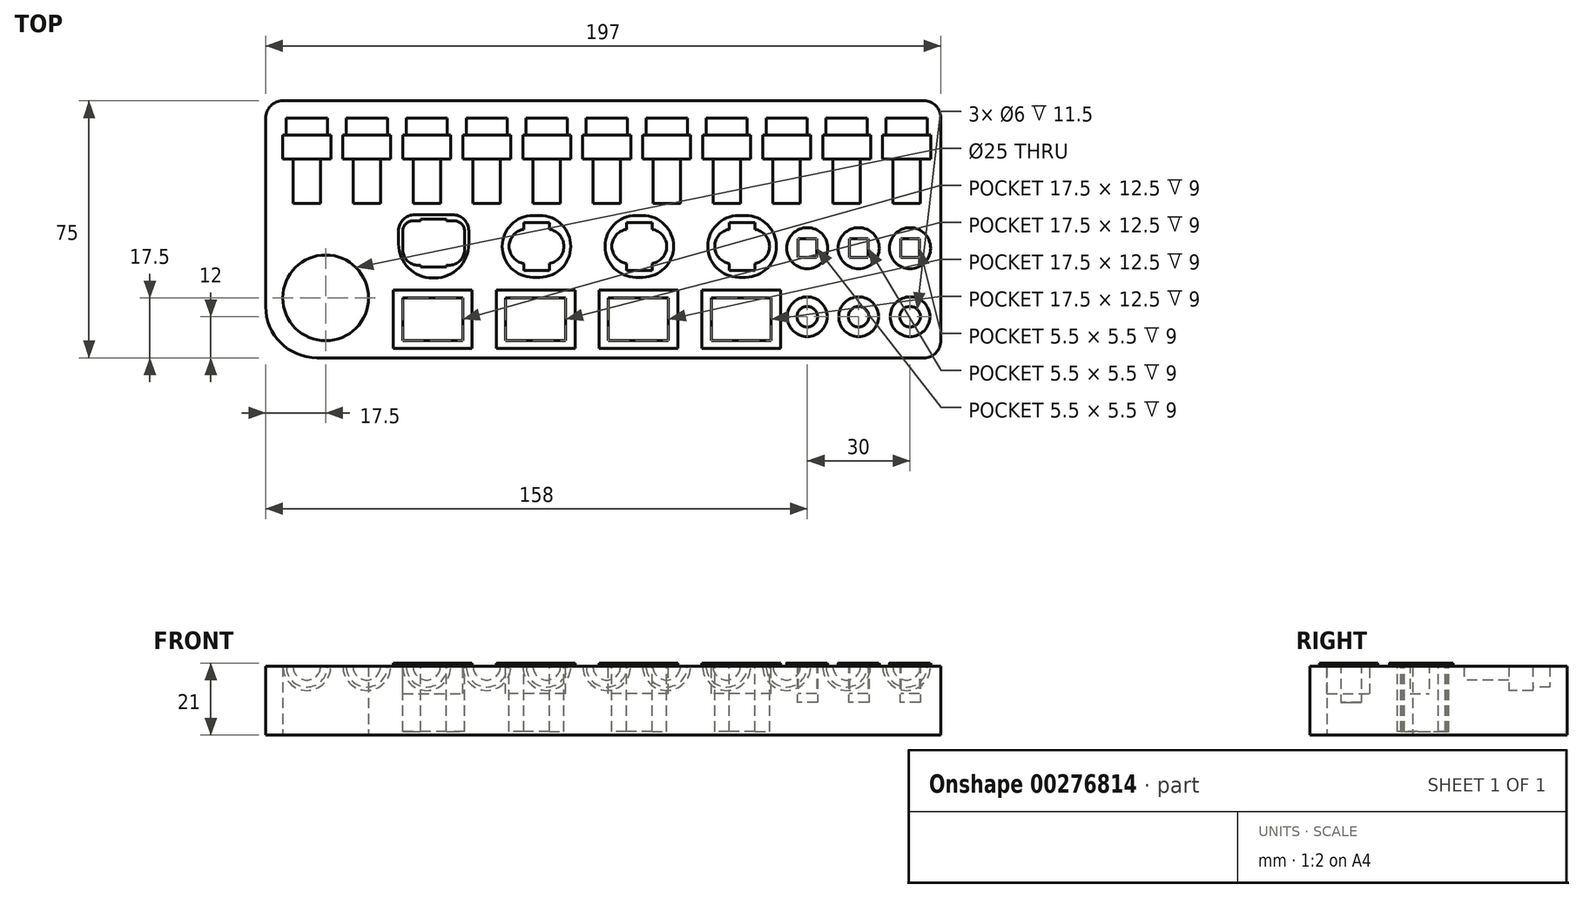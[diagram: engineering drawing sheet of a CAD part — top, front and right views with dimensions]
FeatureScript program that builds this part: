
annotation { "Feature Type Name" : "Feature", "Feature Type Description" : "" }
export const myFeature = defineFeature(function(context is Context, id is Id, definition is map)
    precondition{}
    {
        {
            var Q0;
            Q0=qCreatedBy(makeId("Top.planeOp"),FACE);
            var sketch = newSketch(context, id + "F0", { "sketchPlane" : qUnion([Q0])});
            skLineSegment(sketch, "E0.bottom", {"start": v(15, 0) * mm, "end": v(192, 0) * mm});
            skLineSegment(sketch, "E0.top", {"start": v(5, 75) * mm, "end": v(192, 75) * mm});
            skLineSegment(sketch, "E0.left", {"start": v(0, 15) * mm, "end": v(0, 70) * mm});
            skLineSegment(sketch, "E0.right", {"start": v(197, 5) * mm, "end": v(197, 70) * mm});
            skPoint(sketch, "E1.visualSharp", {"position": v(0, 0) * mm});
            skArc(sketch, "E1.filletArc", {"start": v(0, 15) * mm, "mid": v(4.4, 4.4) * mm, "end": v(15, 0) * mm});
            skPoint(sketch, "E2.visualSharp", {"position": v(0, 75) * mm});
            skArc(sketch, "E2.filletArc", {"start": v(5, 75) * mm, "mid": v(1.46, 73.54) * mm, "end": v(0, 70) * mm});
            skPoint(sketch, "E3.visualSharp", {"position": v(197, 75) * mm});
            skArc(sketch, "E3.filletArc", {"start": v(197, 70) * mm, "mid": v(195.54, 73.54) * mm, "end": v(192, 75) * mm});
            skPoint(sketch, "E4.visualSharp", {"position": v(197, 0) * mm});
            skArc(sketch, "E4.filletArc", {"start": v(192, 0) * mm, "mid": v(195.54, 1.46) * mm, "end": v(197, 5) * mm});
            skLineSegment(sketch, "E5.bottom", {"start": v(0, 0) * mm, "end": v(17.5, 0) * mm, "construction": true});
            skLineSegment(sketch, "E5.top", {"start": v(0, 17.5) * mm, "end": v(17.5, 17.5) * mm, "construction": true});
            skLineSegment(sketch, "E5.left", {"start": v(0, 0) * mm, "end": v(0, 17.5) * mm, "construction": true});
            skLineSegment(sketch, "E5.right", {"start": v(17.5, 0) * mm, "end": v(17.5, 17.5) * mm, "construction": true});
            skCircle(sketch, "E6", {"center": v(17.5, 17.5) * mm, "radius": 12.5 * mm});
            skSolve(sketch);
        }
        {
            var Q0;
            Q0=qSketchRegion(id+"F0",true);
            extrude(context, id + "F1", {"entities" : qUnion([Q0]), "depth" : 20 * mm});
        }
        {
            var Q0;
            Q0=makeQuery(id+"F1.opExtrude","CAP_FACE",FACE,{"disambiguationData":[OSD([sQuery(id+"F0.wireOp",EDGE,"E0.bottom"),sQuery(id+"F0.wireOp",EDGE,"E0.top"),sQuery(id+"F0.wireOp",EDGE,"E0.left"),sQuery(id+"F0.wireOp",EDGE,"E0.right"),sQuery(id+"F0.wireOp",EDGE,"E1.filletArc"),sQuery(id+"F0.wireOp",EDGE,"E2.filletArc"),sQuery(id+"F0.wireOp",EDGE,"E3.filletArc"),sQuery(id+"F0.wireOp",EDGE,"E4.filletArc"),sQuery(id+"F0.wireOp",EDGE,"E6")])],"isStart":false});
            var sketch = newSketch(context, id + "F2", { "sketchPlane" : qUnion([Q0])});
            skLineSegment(sketch, "E7.bottom", {"start": v(0, 0) * mm, "end": v(12, 0) * mm, "construction": true});
            skLineSegment(sketch, "E7.top", {"start": v(0, 70) * mm, "end": v(12, 70) * mm, "construction": true});
            skLineSegment(sketch, "E7.left", {"start": v(0, 0) * mm, "end": v(0, 70) * mm, "construction": true});
            skLineSegment(sketch, "E7.right", {"start": v(12, 0) * mm, "end": v(12, 70) * mm, "construction": true});
            skLineSegment(sketch, "E8", {"start": v(12, 70) * mm, "end": v(29.5, 70) * mm, "construction": true});
            skLineSegment(sketch, "E9", {"start": v(29.5, 70) * mm, "end": v(47, 70) * mm, "construction": true});
            skLineSegment(sketch, "E10", {"start": v(47, 70) * mm, "end": v(64.5, 70) * mm, "construction": true});
            skLineSegment(sketch, "E11", {"start": v(64.5, 70) * mm, "end": v(82, 70) * mm, "construction": true});
            skLineSegment(sketch, "E12", {"start": v(82, 70) * mm, "end": v(99.5, 70) * mm, "construction": true});
            skLineSegment(sketch, "E13", {"start": v(99.5, 70) * mm, "end": v(117, 70) * mm, "construction": true});
            skLineSegment(sketch, "E14", {"start": v(117, 70) * mm, "end": v(134.5, 70) * mm, "construction": true});
            skLineSegment(sketch, "E15", {"start": v(134.5, 70) * mm, "end": v(152, 70) * mm, "construction": true});
            skLineSegment(sketch, "E16", {"start": v(152, 70) * mm, "end": v(169.5, 70) * mm, "construction": true});
            skLineSegment(sketch, "E17", {"start": v(169.5, 70) * mm, "end": v(187, 70) * mm, "construction": true});
            skLineSegment(sketch, "E18.bottom", {"start": v(12, 70) * mm, "end": v(18, 70) * mm});
            skLineSegment(sketch, "E18.left", {"start": v(12, 70) * mm, "end": v(12, 65) * mm});
            skLineSegment(sketch, "E18.right", {"start": v(18, 70) * mm, "end": v(18, 65) * mm});
            skLineSegment(sketch, "E19.bottom", {"start": v(29.5, 70) * mm, "end": v(35.5, 70) * mm});
            skLineSegment(sketch, "E19.left", {"start": v(29.5, 70) * mm, "end": v(29.5, 65) * mm});
            skLineSegment(sketch, "E19.right", {"start": v(35.5, 70) * mm, "end": v(35.5, 65) * mm});
            skLineSegment(sketch, "E20.bottom", {"start": v(47, 70) * mm, "end": v(53, 70) * mm});
            skLineSegment(sketch, "E20.left", {"start": v(47, 70) * mm, "end": v(47, 65) * mm});
            skLineSegment(sketch, "E20.right", {"start": v(53, 70) * mm, "end": v(53, 65) * mm});
            skLineSegment(sketch, "E21.bottom", {"start": v(64.5, 70) * mm, "end": v(70.5, 70) * mm});
            skLineSegment(sketch, "E21.left", {"start": v(64.5, 70) * mm, "end": v(64.5, 65) * mm});
            skLineSegment(sketch, "E21.right", {"start": v(70.5, 70) * mm, "end": v(70.5, 65) * mm});
            skLineSegment(sketch, "E22.bottom", {"start": v(82, 70) * mm, "end": v(88, 70) * mm});
            skLineSegment(sketch, "E22.left", {"start": v(82, 70) * mm, "end": v(82, 65) * mm});
            skLineSegment(sketch, "E22.right", {"start": v(88, 70) * mm, "end": v(88, 65) * mm});
            skLineSegment(sketch, "E23.bottom", {"start": v(99.5, 70) * mm, "end": v(105.5, 70) * mm});
            skLineSegment(sketch, "E23.left", {"start": v(99.5, 70) * mm, "end": v(99.5, 65) * mm});
            skLineSegment(sketch, "E23.right", {"start": v(105.5, 70) * mm, "end": v(105.5, 65) * mm});
            skLineSegment(sketch, "E24.bottom", {"start": v(117, 70) * mm, "end": v(123, 70) * mm});
            skLineSegment(sketch, "E24.left", {"start": v(117, 70) * mm, "end": v(117, 65) * mm});
            skLineSegment(sketch, "E24.right", {"start": v(123, 70) * mm, "end": v(123, 65) * mm});
            skLineSegment(sketch, "E25.bottom", {"start": v(134.5, 70) * mm, "end": v(140.5, 70) * mm});
            skLineSegment(sketch, "E25.left", {"start": v(134.5, 70) * mm, "end": v(134.5, 65) * mm});
            skLineSegment(sketch, "E25.right", {"start": v(140.5, 70) * mm, "end": v(140.5, 65) * mm});
            skLineSegment(sketch, "E26.bottom", {"start": v(152, 70) * mm, "end": v(158, 70) * mm});
            skLineSegment(sketch, "E26.left", {"start": v(152, 70) * mm, "end": v(152, 65) * mm});
            skLineSegment(sketch, "E26.right", {"start": v(158, 70) * mm, "end": v(158, 65) * mm});
            skLineSegment(sketch, "E27.bottom", {"start": v(169.5, 70) * mm, "end": v(175.5, 70) * mm});
            skLineSegment(sketch, "E27.left", {"start": v(169.5, 70) * mm, "end": v(169.5, 65) * mm});
            skLineSegment(sketch, "E27.right", {"start": v(175.5, 70) * mm, "end": v(175.5, 65) * mm});
            skLineSegment(sketch, "E28.bottom", {"start": v(187, 70) * mm, "end": v(193, 70) * mm});
            skLineSegment(sketch, "E28.left", {"start": v(187, 70) * mm, "end": v(187, 65) * mm});
            skLineSegment(sketch, "E28.right", {"start": v(193, 70) * mm, "end": v(193, 65) * mm});
            skLineSegment(sketch, "E29.bottom", {"start": v(18, 65) * mm, "end": v(19, 65) * mm});
            skLineSegment(sketch, "E29.top", {"start": v(16, 58) * mm, "end": v(19, 58) * mm});
            skLineSegment(sketch, "E29.left", {"start": v(12, 65) * mm, "end": v(12, 58) * mm});
            skLineSegment(sketch, "E29.right", {"start": v(19, 65) * mm, "end": v(19, 58) * mm});
            skLineSegment(sketch, "E30.bottom", {"start": v(35.5, 65) * mm, "end": v(36.5, 65) * mm});
            skLineSegment(sketch, "E30.top", {"start": v(33.5, 58) * mm, "end": v(36.5, 58) * mm});
            skLineSegment(sketch, "E30.left", {"start": v(29.5, 65) * mm, "end": v(29.5, 58) * mm});
            skLineSegment(sketch, "E30.right", {"start": v(36.5, 65) * mm, "end": v(36.5, 58) * mm});
            skLineSegment(sketch, "E31.bottom", {"start": v(53, 65) * mm, "end": v(54, 65) * mm});
            skLineSegment(sketch, "E31.top", {"start": v(51, 58) * mm, "end": v(54, 58) * mm});
            skLineSegment(sketch, "E31.left", {"start": v(47, 65) * mm, "end": v(47, 58) * mm});
            skLineSegment(sketch, "E31.right", {"start": v(54, 65) * mm, "end": v(54, 58) * mm});
            skLineSegment(sketch, "E32.bottom", {"start": v(70.5, 65) * mm, "end": v(71.5, 65) * mm});
            skLineSegment(sketch, "E32.top", {"start": v(68.5, 58) * mm, "end": v(71.5, 58) * mm});
            skLineSegment(sketch, "E32.left", {"start": v(64.5, 65) * mm, "end": v(64.5, 58) * mm});
            skLineSegment(sketch, "E32.right", {"start": v(71.5, 65) * mm, "end": v(71.5, 58) * mm});
            skLineSegment(sketch, "E33.bottom", {"start": v(88, 65) * mm, "end": v(89, 65) * mm});
            skLineSegment(sketch, "E33.top", {"start": v(86, 58) * mm, "end": v(89, 58) * mm});
            skLineSegment(sketch, "E33.left", {"start": v(82, 65) * mm, "end": v(82, 58) * mm});
            skLineSegment(sketch, "E33.right", {"start": v(89, 65) * mm, "end": v(89, 58) * mm});
            skLineSegment(sketch, "E34.bottom", {"start": v(105.5, 65) * mm, "end": v(106.5, 65) * mm});
            skLineSegment(sketch, "E34.top", {"start": v(103.5, 58) * mm, "end": v(106.5, 58) * mm});
            skLineSegment(sketch, "E34.left", {"start": v(99.5, 65) * mm, "end": v(99.5, 58) * mm});
            skLineSegment(sketch, "E34.right", {"start": v(106.5, 65) * mm, "end": v(106.5, 58) * mm});
            skLineSegment(sketch, "E35.bottom", {"start": v(123, 65) * mm, "end": v(124, 65) * mm});
            skLineSegment(sketch, "E35.top", {"start": v(121, 58) * mm, "end": v(124, 58) * mm});
            skLineSegment(sketch, "E35.left", {"start": v(117, 65) * mm, "end": v(117, 58) * mm});
            skLineSegment(sketch, "E35.right", {"start": v(124, 65) * mm, "end": v(124, 58) * mm});
            skLineSegment(sketch, "E36.bottom", {"start": v(140.5, 65) * mm, "end": v(141.5, 65) * mm});
            skLineSegment(sketch, "E36.top", {"start": v(138.5, 58) * mm, "end": v(141.5, 58) * mm});
            skLineSegment(sketch, "E36.left", {"start": v(134.5, 65) * mm, "end": v(134.5, 58) * mm});
            skLineSegment(sketch, "E36.right", {"start": v(141.5, 65) * mm, "end": v(141.5, 58) * mm});
            skLineSegment(sketch, "E37.top", {"start": v(156, 58) * mm, "end": v(159, 58) * mm});
            skLineSegment(sketch, "E37.left", {"start": v(152, 65) * mm, "end": v(152, 58) * mm});
            skLineSegment(sketch, "E37.right", {"start": v(159, 65) * mm, "end": v(159, 58) * mm});
            skLineSegment(sketch, "E38.bottom", {"start": v(175.5, 65) * mm, "end": v(176.5, 65) * mm});
            skLineSegment(sketch, "E38.top", {"start": v(173.5, 58) * mm, "end": v(176.5, 58) * mm});
            skLineSegment(sketch, "E38.left", {"start": v(169.5, 65) * mm, "end": v(169.5, 58) * mm});
            skLineSegment(sketch, "E38.right", {"start": v(176.5, 65) * mm, "end": v(176.5, 58) * mm});
            skLineSegment(sketch, "E39.bottom", {"start": v(193, 65) * mm, "end": v(194, 65) * mm});
            skLineSegment(sketch, "E39.top", {"start": v(191, 58) * mm, "end": v(194, 58) * mm});
            skLineSegment(sketch, "E39.left", {"start": v(187, 65) * mm, "end": v(187, 58) * mm});
            skLineSegment(sketch, "E39.right", {"start": v(194, 65) * mm, "end": v(194, 58) * mm});
            skLineSegment(sketch, "E40.top", {"start": v(12, 45) * mm, "end": v(16, 45) * mm});
            skLineSegment(sketch, "E40.left", {"start": v(12, 58) * mm, "end": v(12, 45) * mm});
            skLineSegment(sketch, "E40.right", {"start": v(16, 58) * mm, "end": v(16, 45) * mm});
            skLineSegment(sketch, "E41.top", {"start": v(29.5, 45) * mm, "end": v(33.5, 45) * mm});
            skLineSegment(sketch, "E41.left", {"start": v(29.5, 58) * mm, "end": v(29.5, 45) * mm});
            skLineSegment(sketch, "E41.right", {"start": v(33.5, 58) * mm, "end": v(33.5, 45) * mm});
            skLineSegment(sketch, "E42.top", {"start": v(47, 45) * mm, "end": v(51, 45) * mm});
            skLineSegment(sketch, "E42.left", {"start": v(47, 58) * mm, "end": v(47, 45) * mm});
            skLineSegment(sketch, "E42.right", {"start": v(51, 58) * mm, "end": v(51, 45) * mm});
            skLineSegment(sketch, "E43.top", {"start": v(64.5, 45) * mm, "end": v(68.5, 45) * mm});
            skLineSegment(sketch, "E43.left", {"start": v(64.5, 58) * mm, "end": v(64.5, 45) * mm});
            skLineSegment(sketch, "E43.right", {"start": v(68.5, 58) * mm, "end": v(68.5, 45) * mm});
            skLineSegment(sketch, "E44.top", {"start": v(82, 45) * mm, "end": v(86, 45) * mm});
            skLineSegment(sketch, "E44.left", {"start": v(82, 58) * mm, "end": v(82, 45) * mm});
            skLineSegment(sketch, "E44.right", {"start": v(86, 58) * mm, "end": v(86, 45) * mm});
            skLineSegment(sketch, "E45.top", {"start": v(99.5, 45) * mm, "end": v(103.5, 45) * mm});
            skLineSegment(sketch, "E45.left", {"start": v(99.5, 58) * mm, "end": v(99.5, 45) * mm});
            skLineSegment(sketch, "E45.right", {"start": v(103.5, 58) * mm, "end": v(103.5, 45) * mm});
            skLineSegment(sketch, "E46.top", {"start": v(117, 45) * mm, "end": v(121, 45) * mm});
            skLineSegment(sketch, "E46.left", {"start": v(117, 58) * mm, "end": v(117, 45) * mm});
            skLineSegment(sketch, "E46.right", {"start": v(121, 58) * mm, "end": v(121, 45) * mm});
            skLineSegment(sketch, "E47.top", {"start": v(134.5, 45) * mm, "end": v(138.5, 45) * mm});
            skLineSegment(sketch, "E47.left", {"start": v(134.5, 58) * mm, "end": v(134.5, 45) * mm});
            skLineSegment(sketch, "E47.right", {"start": v(138.5, 58) * mm, "end": v(138.5, 45) * mm});
            skLineSegment(sketch, "E48.top", {"start": v(152, 45) * mm, "end": v(156, 45) * mm});
            skLineSegment(sketch, "E48.left", {"start": v(152, 58) * mm, "end": v(152, 45) * mm});
            skLineSegment(sketch, "E48.right", {"start": v(156, 58) * mm, "end": v(156, 45) * mm});
            skLineSegment(sketch, "E49.top", {"start": v(169.5, 45) * mm, "end": v(173.5, 45) * mm});
            skLineSegment(sketch, "E49.left", {"start": v(169.5, 58) * mm, "end": v(169.5, 45) * mm});
            skLineSegment(sketch, "E49.right", {"start": v(173.5, 58) * mm, "end": v(173.5, 45) * mm});
            skLineSegment(sketch, "E50.top", {"start": v(187, 45) * mm, "end": v(191, 45) * mm});
            skLineSegment(sketch, "E50.left", {"start": v(187, 58) * mm, "end": v(187, 45) * mm});
            skLineSegment(sketch, "E50.right", {"start": v(191, 58) * mm, "end": v(191, 45) * mm});
            skLineSegment(sketch, "E51", {"start": v(158, 65) * mm, "end": v(159, 65) * mm});
            skSolve(sketch);
        }
        {
            var Q0;
            Q0=makeQuery(id+"F2.imprint","IMPRINT",FACE,{"disambiguationData":[TD([[makeQuery(id+"F2.imprint","IMPRINT",EDGE,{"derivedFrom":sQuery(id+"F2.wireOp",EDGE,"E18.bottom")}),-1.0]])]});
            var Q1;
            Q1=sQuery(id+"F2.wireOp",EDGE,"E40.left");
            revolve(context, id + "F3", {"operationType" : NewBodyOperationType.REMOVE, "entities" : qUnion([Q0]), "axis" : qUnion([Q1]), "revolveType" : RevolveType.FULL, "oppositeDirection" : true});
        }
        {
            var Q0;
            Q0=makeQuery(id+"F2.imprint","IMPRINT",FACE,{"disambiguationData":[TD([[makeQuery(id+"F2.imprint","IMPRINT",EDGE,{"derivedFrom":sQuery(id+"F2.wireOp",EDGE,"E19.bottom")}),-1.0]])]});
            var Q1;
            Q1=sQuery(id+"F2.wireOp",EDGE,"E41.left");
            revolve(context, id + "F4", {"operationType" : NewBodyOperationType.REMOVE, "entities" : qUnion([Q0]), "axis" : qUnion([Q1]), "revolveType" : RevolveType.FULL, "oppositeDirection" : true});
        }
        {
            var Q0;
            Q0=makeQuery(id+"F2.imprint","IMPRINT",FACE,{"disambiguationData":[TD([[makeQuery(id+"F2.imprint","IMPRINT",EDGE,{"derivedFrom":sQuery(id+"F2.wireOp",EDGE,"E20.bottom")}),-1.0]])]});
            var Q1;
            Q1=sQuery(id+"F2.wireOp",EDGE,"E42.left");
            revolve(context, id + "F5", {"operationType" : NewBodyOperationType.REMOVE, "entities" : qUnion([Q0]), "axis" : qUnion([Q1]), "revolveType" : RevolveType.FULL, "oppositeDirection" : true});
        }
        {
            var Q0;
            Q0=makeQuery(id+"F2.imprint","IMPRINT",FACE,{"disambiguationData":[TD([[makeQuery(id+"F2.imprint","IMPRINT",EDGE,{"derivedFrom":sQuery(id+"F2.wireOp",EDGE,"E21.bottom")}),-1.0]])]});
            var Q1;
            Q1=sQuery(id+"F2.wireOp",EDGE,"E43.left");
            revolve(context, id + "F6", {"operationType" : NewBodyOperationType.REMOVE, "entities" : qUnion([Q0]), "axis" : qUnion([Q1]), "revolveType" : RevolveType.FULL, "oppositeDirection" : true});
        }
        {
            var Q0;
            Q0=makeQuery(id+"F2.imprint","IMPRINT",FACE,{"disambiguationData":[TD([[makeQuery(id+"F2.imprint","IMPRINT",EDGE,{"derivedFrom":sQuery(id+"F2.wireOp",EDGE,"E22.bottom")}),-1.0]])]});
            var Q1;
            Q1=sQuery(id+"F2.wireOp",EDGE,"E44.left");
            revolve(context, id + "F7", {"operationType" : NewBodyOperationType.REMOVE, "entities" : qUnion([Q0]), "axis" : qUnion([Q1]), "revolveType" : RevolveType.FULL, "oppositeDirection" : true});
        }
        {
            var Q0;
            Q0=makeQuery(id+"F2.imprint","IMPRINT",FACE,{"disambiguationData":[TD([[makeQuery(id+"F2.imprint","IMPRINT",EDGE,{"derivedFrom":sQuery(id+"F2.wireOp",EDGE,"E23.bottom")}),-1.0]])]});
            var Q1;
            Q1=sQuery(id+"F2.wireOp",EDGE,"E45.left");
            revolve(context, id + "F8", {"operationType" : NewBodyOperationType.REMOVE, "entities" : qUnion([Q0]), "axis" : qUnion([Q1]), "revolveType" : RevolveType.FULL, "oppositeDirection" : true});
        }
        {
            var Q0;
            Q0=makeQuery(id+"F2.imprint","IMPRINT",FACE,{"disambiguationData":[TD([[makeQuery(id+"F2.imprint","IMPRINT",EDGE,{"derivedFrom":sQuery(id+"F2.wireOp",EDGE,"E24.bottom")}),-1.0]])]});
            var Q1;
            Q1=sQuery(id+"F2.wireOp",EDGE,"E46.left");
            revolve(context, id + "F9", {"operationType" : NewBodyOperationType.REMOVE, "entities" : qUnion([Q0]), "axis" : qUnion([Q1]), "revolveType" : RevolveType.FULL, "oppositeDirection" : true});
        }
        {
            var Q0;
            Q0=makeQuery(id+"F2.imprint","IMPRINT",FACE,{"disambiguationData":[TD([[makeQuery(id+"F2.imprint","IMPRINT",EDGE,{"derivedFrom":sQuery(id+"F2.wireOp",EDGE,"E25.bottom")}),-1.0]])]});
            var Q1;
            Q1=sQuery(id+"F2.wireOp",EDGE,"E47.left");
            revolve(context, id + "F10", {"operationType" : NewBodyOperationType.REMOVE, "entities" : qUnion([Q0]), "axis" : qUnion([Q1]), "revolveType" : RevolveType.FULL, "oppositeDirection" : true});
        }
        {
            var Q0;
            Q0=makeQuery(id+"F2.imprint","IMPRINT",FACE,{"disambiguationData":[TD([[makeQuery(id+"F2.imprint","IMPRINT",EDGE,{"derivedFrom":sQuery(id+"F2.wireOp",EDGE,"E27.bottom")}),-1.0]])]});
            var Q1;
            Q1=sQuery(id+"F2.wireOp",EDGE,"E49.left");
            revolve(context, id + "F11", {"operationType" : NewBodyOperationType.REMOVE, "entities" : qUnion([Q0]), "axis" : qUnion([Q1]), "revolveType" : RevolveType.FULL, "oppositeDirection" : true});
        }
        {
            var Q0;
            Q0=makeQuery(id+"F2.imprint","IMPRINT",FACE,{"disambiguationData":[TD([[makeQuery(id+"F2.imprint","IMPRINT",EDGE,{"derivedFrom":sQuery(id+"F2.wireOp",EDGE,"E26.bottom")}),-1.0]])]});
            var Q1;
            Q1=sQuery(id+"F2.wireOp",EDGE,"E48.left");
            revolve(context, id + "F12", {"operationType" : NewBodyOperationType.REMOVE, "entities" : qUnion([Q0]), "axis" : qUnion([Q1]), "revolveType" : RevolveType.FULL, "oppositeDirection" : true});
        }
        {
            var Q0;
            Q0=makeQuery(id+"F2.imprint","IMPRINT",FACE,{"disambiguationData":[TD([[makeQuery(id+"F2.imprint","IMPRINT",EDGE,{"derivedFrom":sQuery(id+"F2.wireOp",EDGE,"E28.bottom")}),-1.0]])]});
            var Q1;
            Q1=sQuery(id+"F2.wireOp",EDGE,"E50.left");
            revolve(context, id + "F13", {"operationType" : NewBodyOperationType.REMOVE, "entities" : qUnion([Q0]), "axis" : qUnion([Q1]), "revolveType" : RevolveType.FULL, "oppositeDirection" : true});
        }
        {
            var Q0;
            Q0=makeQuery(id+"F1.opExtrude","CAP_FACE",FACE,{"disambiguationData":[OSD([sQuery(id+"F0.wireOp",EDGE,"E0.bottom"),sQuery(id+"F0.wireOp",EDGE,"E0.top"),sQuery(id+"F0.wireOp",EDGE,"E0.left"),sQuery(id+"F0.wireOp",EDGE,"E0.right"),sQuery(id+"F0.wireOp",EDGE,"E1.filletArc"),sQuery(id+"F0.wireOp",EDGE,"E2.filletArc"),sQuery(id+"F0.wireOp",EDGE,"E3.filletArc"),sQuery(id+"F0.wireOp",EDGE,"E4.filletArc"),sQuery(id+"F0.wireOp",EDGE,"E6")])],"isStart":false});
            var sketch = newSketch(context, id + "F14", { "sketchPlane" : qUnion([Q0])});
            skLineSegment(sketch, "E52.bottom", {"start": v(0, 0) * mm, "end": v(40, 0) * mm, "construction": true});
            skLineSegment(sketch, "E52.top", {"start": v(0, 5) * mm, "end": v(40, 5) * mm, "construction": true});
            skLineSegment(sketch, "E52.left", {"start": v(0, 0) * mm, "end": v(0, 5) * mm, "construction": true});
            skLineSegment(sketch, "E52.right", {"start": v(40, 0) * mm, "end": v(40, 5) * mm, "construction": true});
            skLineSegment(sketch, "E53.bottom", {"start": v(40, 5) * mm, "end": v(57.5, 5) * mm});
            skLineSegment(sketch, "E53.top", {"start": v(40, 17.5) * mm, "end": v(57.5, 17.5) * mm});
            skLineSegment(sketch, "E53.left", {"start": v(40, 5) * mm, "end": v(40, 17.5) * mm});
            skLineSegment(sketch, "E53.right", {"start": v(57.5, 5) * mm, "end": v(57.5, 17.5) * mm});
            skLineSegment(sketch, "E54", {"start": v(57.5, 17.5) * mm, "end": v(87.5, 17.5) * mm, "construction": true});
            skLineSegment(sketch, "E55", {"start": v(87.5, 17.5) * mm, "end": v(117.5, 17.5) * mm, "construction": true});
            skLineSegment(sketch, "E56", {"start": v(117.5, 17.5) * mm, "end": v(147.5, 17.5) * mm, "construction": true});
            skLineSegment(sketch, "E57.bottom", {"start": v(87.5, 17.5) * mm, "end": v(70, 17.5) * mm});
            skLineSegment(sketch, "E57.top", {"start": v(87.5, 5) * mm, "end": v(70, 5) * mm});
            skLineSegment(sketch, "E57.left", {"start": v(87.5, 17.5) * mm, "end": v(87.5, 5) * mm});
            skLineSegment(sketch, "E57.right", {"start": v(70, 17.5) * mm, "end": v(70, 5) * mm});
            skLineSegment(sketch, "E58.bottom", {"start": v(117.5, 17.5) * mm, "end": v(100, 17.5) * mm});
            skLineSegment(sketch, "E58.top", {"start": v(117.5, 5) * mm, "end": v(100, 5) * mm});
            skLineSegment(sketch, "E58.left", {"start": v(117.5, 17.5) * mm, "end": v(117.5, 5) * mm});
            skLineSegment(sketch, "E58.right", {"start": v(100, 17.5) * mm, "end": v(100, 5) * mm});
            skLineSegment(sketch, "E59.bottom", {"start": v(147.5, 17.5) * mm, "end": v(130, 17.5) * mm});
            skLineSegment(sketch, "E59.top", {"start": v(147.5, 5) * mm, "end": v(130, 5) * mm});
            skLineSegment(sketch, "E59.left", {"start": v(147.5, 17.5) * mm, "end": v(147.5, 5) * mm});
            skLineSegment(sketch, "E59.right", {"start": v(130, 17.5) * mm, "end": v(130, 5) * mm});
            skLineSegment(sketch, "E60", {"start": v(40, 5) * mm, "end": v(57.5, 17.5) * mm, "construction": true});
            skLineSegment(sketch, "E61", {"start": v(70, 17.5) * mm, "end": v(87.5, 5) * mm, "construction": true});
            skLineSegment(sketch, "E62", {"start": v(100, 5) * mm, "end": v(117.5, 17.5) * mm, "construction": true});
            skLineSegment(sketch, "E63", {"start": v(130, 17.5) * mm, "end": v(147.5, 5) * mm, "construction": true});
            skLineSegment(sketch, "E64.bottom", {"start": v(60.25, 2.75) * mm, "end": v(37.25, 2.75) * mm});
            skLineSegment(sketch, "E64.top", {"start": v(60.25, 19.75) * mm, "end": v(37.25, 19.75) * mm});
            skLineSegment(sketch, "E64.left", {"start": v(60.25, 2.75) * mm, "end": v(60.25, 19.75) * mm});
            skLineSegment(sketch, "E64.right", {"start": v(37.25, 2.75) * mm, "end": v(37.25, 19.75) * mm});
            skPoint(sketch, "E64.middle", {"position": v(48.75, 11.25) * mm});
            skLineSegment(sketch, "E65.bottom", {"start": v(67.25, 2.75) * mm, "end": v(90.25, 2.75) * mm});
            skLineSegment(sketch, "E65.top", {"start": v(67.25, 19.75) * mm, "end": v(90.25, 19.75) * mm});
            skLineSegment(sketch, "E65.left", {"start": v(67.25, 2.75) * mm, "end": v(67.25, 19.75) * mm});
            skLineSegment(sketch, "E65.right", {"start": v(90.25, 2.75) * mm, "end": v(90.25, 19.75) * mm});
            skPoint(sketch, "E65.middle", {"position": v(78.75, 11.25) * mm});
            skLineSegment(sketch, "E66.bottom", {"start": v(97.25, 19.75) * mm, "end": v(120.25, 19.75) * mm});
            skLineSegment(sketch, "E66.top", {"start": v(97.25, 2.75) * mm, "end": v(120.25, 2.75) * mm});
            skLineSegment(sketch, "E66.left", {"start": v(97.25, 19.75) * mm, "end": v(97.25, 2.75) * mm});
            skLineSegment(sketch, "E66.right", {"start": v(120.25, 19.75) * mm, "end": v(120.25, 2.75) * mm});
            skPoint(sketch, "E66.middle", {"position": v(108.75, 11.25) * mm});
            skLineSegment(sketch, "E67.bottom", {"start": v(127.25, 2.75) * mm, "end": v(150.25, 2.75) * mm});
            skLineSegment(sketch, "E67.top", {"start": v(127.25, 19.75) * mm, "end": v(150.25, 19.75) * mm});
            skLineSegment(sketch, "E67.left", {"start": v(127.25, 2.75) * mm, "end": v(127.25, 19.75) * mm});
            skLineSegment(sketch, "E67.right", {"start": v(150.25, 2.75) * mm, "end": v(150.25, 19.75) * mm});
            skPoint(sketch, "E67.middle", {"position": v(138.75, 11.25) * mm});
            skSolve(sketch);
        }
        {
            var Q0;
            Q0=makeQuery(id+"F14.imprint","IMPRINT",FACE,{"disambiguationData":[TD([[makeQuery(id+"F14.imprint","IMPRINT",EDGE,{"derivedFrom":sQuery(id+"F14.wireOp",EDGE,"E53.bottom")}),1.0]])]});
            var Q1;
            Q1=makeQuery(id+"F14.imprint","IMPRINT",FACE,{"disambiguationData":[TD([[makeQuery(id+"F14.imprint","IMPRINT",EDGE,{"derivedFrom":sQuery(id+"F14.wireOp",EDGE,"E57.bottom")}),1.0]])]});
            var Q2;
            Q2=makeQuery(id+"F14.imprint","IMPRINT",FACE,{"disambiguationData":[TD([[makeQuery(id+"F14.imprint","IMPRINT",EDGE,{"derivedFrom":sQuery(id+"F14.wireOp",EDGE,"E58.bottom")}),1.0]])]});
            var Q3;
            Q3=makeQuery(id+"F14.imprint","IMPRINT",FACE,{"disambiguationData":[TD([[makeQuery(id+"F14.imprint","IMPRINT",EDGE,{"derivedFrom":sQuery(id+"F14.wireOp",EDGE,"E59.bottom")}),1.0]])]});
            extrude(context, id + "F15", {"entities" : qUnion([Q0, Q1, Q2, Q3]), "operationType" : NewBodyOperationType.REMOVE, "oppositeDirection" : true, "depth" : 8 * mm});
        }
        {
            var Q0;
            Q0=makeQuery(id+"F14.imprint","IMPRINT",FACE,{"disambiguationData":[TD([[makeQuery(id+"F14.imprint","IMPRINT",EDGE,{"derivedFrom":sQuery(id+"F14.wireOp",EDGE,"E57.bottom")}),-1.0]])]});
            var Q1;
            Q1=makeQuery(id+"F14.imprint","IMPRINT",FACE,{"disambiguationData":[TD([[makeQuery(id+"F14.imprint","IMPRINT",EDGE,{"derivedFrom":sQuery(id+"F14.wireOp",EDGE,"E58.bottom")}),-1.0]])]});
            var Q2;
            Q2=makeQuery(id+"F14.imprint","IMPRINT",FACE,{"disambiguationData":[TD([[makeQuery(id+"F14.imprint","IMPRINT",EDGE,{"derivedFrom":sQuery(id+"F14.wireOp",EDGE,"E59.bottom")}),-1.0]])]});
            var Q3;
            Q3=makeQuery(id+"F14.imprint","IMPRINT",FACE,{"disambiguationData":[TD([[makeQuery(id+"F14.imprint","IMPRINT",EDGE,{"derivedFrom":sQuery(id+"F14.wireOp",EDGE,"E53.bottom")}),-1.0]])]});
            extrude(context, id + "F16", {"entities" : qUnion([Q0, Q1, Q2, Q3]), "operationType" : NewBodyOperationType.ADD, "depth" : 1 * mm});
        }
        {
            var Q0;
            Q0=makeQuery(id+"F1.opExtrude","CAP_FACE",FACE,{"disambiguationData":[OSD([sQuery(id+"F0.wireOp",EDGE,"E0.bottom"),sQuery(id+"F0.wireOp",EDGE,"E0.top"),sQuery(id+"F0.wireOp",EDGE,"E0.left"),sQuery(id+"F0.wireOp",EDGE,"E0.right"),sQuery(id+"F0.wireOp",EDGE,"E1.filletArc"),sQuery(id+"F0.wireOp",EDGE,"E2.filletArc"),sQuery(id+"F0.wireOp",EDGE,"E3.filletArc"),sQuery(id+"F0.wireOp",EDGE,"E4.filletArc"),sQuery(id+"F0.wireOp",EDGE,"E6")])],"isStart":false});
            var sketch = newSketch(context, id + "F17", { "sketchPlane" : qUnion([Q0])});
            skLineSegment(sketch, "E68.bottom", {"start": v(0, 0) * mm, "end": v(40, 0) * mm, "construction": true});
            skLineSegment(sketch, "E68.top", {"start": v(0, 27) * mm, "end": v(40, 27) * mm, "construction": true});
            skLineSegment(sketch, "E68.left", {"start": v(0, 0) * mm, "end": v(0, 27) * mm, "construction": true});
            skLineSegment(sketch, "E68.right", {"start": v(40, 0) * mm, "end": v(40, 27) * mm, "construction": true});
            skLineSegment(sketch, "E69.bottom", {"start": v(44.5, 27) * mm, "end": v(45.25, 27) * mm});
            skLineSegment(sketch, "E69.top", {"start": v(43, 40) * mm, "end": v(45.25, 40) * mm});
            skLineSegment(sketch, "E69.left", {"start": v(40, 31.5) * mm, "end": v(40, 37) * mm});
            skLineSegment(sketch, "E69.right", {"start": v(58, 31.5) * mm, "end": v(58, 37) * mm});
            skLineSegment(sketch, "E70.bottom", {"start": v(49.25, 23.27) * mm, "end": v(48.75, 23.27) * mm});
            skLineSegment(sketch, "E70.top", {"start": v(54.5, 41.77) * mm, "end": v(43.5, 41.77) * mm});
            skLineSegment(sketch, "E70.left", {"start": v(59.25, 33.27) * mm, "end": v(59.25, 37.02) * mm});
            skLineSegment(sketch, "E70.right", {"start": v(38.75, 33.27) * mm, "end": v(38.75, 37.02) * mm});
            skPoint(sketch, "E70.middle", {"position": v(49, 32.52) * mm});
            skPoint(sketch, "E71.visualSharp", {"position": v(38.75, 41.77) * mm});
            skArc(sketch, "E71.filletArc", {"start": v(43.5, 41.77) * mm, "mid": v(40.14, 40.38) * mm, "end": v(38.75, 37.02) * mm});
            skPoint(sketch, "E72.visualSharp", {"position": v(59.25, 41.77) * mm});
            skArc(sketch, "E72.filletArc", {"start": v(59.25, 37.02) * mm, "mid": v(57.86, 40.38) * mm, "end": v(54.5, 41.77) * mm});
            skPoint(sketch, "E73.visualSharp", {"position": v(59.25, 23.27) * mm});
            skArc(sketch, "E73.filletArc", {"start": v(49.25, 23.27) * mm, "mid": v(56.32, 26.2) * mm, "end": v(59.25, 33.27) * mm});
            skPoint(sketch, "E74.visualSharp", {"position": v(38.75, 23.27) * mm});
            skArc(sketch, "E74.filletArc", {"start": v(38.75, 33.27) * mm, "mid": v(41.68, 26.2) * mm, "end": v(48.75, 23.27) * mm});
            skPoint(sketch, "E75.visualSharp", {"position": v(40, 40) * mm});
            skArc(sketch, "E75.filletArc", {"start": v(43, 40) * mm, "mid": v(40.88, 39.12) * mm, "end": v(40, 37) * mm});
            skPoint(sketch, "E76.visualSharp", {"position": v(58, 40) * mm});
            skArc(sketch, "E76.filletArc", {"start": v(58, 37) * mm, "mid": v(57.12, 39.12) * mm, "end": v(55, 40) * mm});
            skPoint(sketch, "E77.visualSharp", {"position": v(58, 27) * mm});
            skArc(sketch, "E77.filletArc", {"start": v(53.5, 27) * mm, "mid": v(56.68, 28.32) * mm, "end": v(58, 31.5) * mm});
            skPoint(sketch, "E78.visualSharp", {"position": v(40, 27) * mm});
            skArc(sketch, "E78.filletArc", {"start": v(40, 31.5) * mm, "mid": v(41.32, 28.32) * mm, "end": v(44.5, 27) * mm});
            skLineSegment(sketch, "E79", {"start": v(38.75, 37.02) * mm, "end": v(40, 37) * mm, "construction": true});
            skLineSegment(sketch, "E80", {"start": v(49, 32.52) * mm, "end": v(79, 32.52) * mm, "construction": true});
            skLineSegment(sketch, "E81", {"start": v(79, 32.52) * mm, "end": v(109, 32.52) * mm, "construction": true});
            skLineSegment(sketch, "E82", {"start": v(109, 32.52) * mm, "end": v(139, 32.52) * mm, "construction": true});
            skLineSegment(sketch, "E83.bottom", {"start": v(82.75, 39.52) * mm, "end": v(75.25, 39.52) * mm});
            skLineSegment(sketch, "E83.top", {"start": v(82.75, 25.52) * mm, "end": v(75.25, 25.52) * mm});
            skLineSegment(sketch, "E83.left", {"start": v(82.75, 39.52) * mm, "end": v(82.75, 37.47) * mm});
            skLineSegment(sketch, "E83.right", {"start": v(75.25, 39.52) * mm, "end": v(75.25, 37.47) * mm});
            skPoint(sketch, "E83.middle", {"position": v(79, 32.52) * mm});
            skLineSegment(sketch, "E84.bottom", {"start": v(112.75, 39.52) * mm, "end": v(105.25, 39.52) * mm});
            skLineSegment(sketch, "E84.top", {"start": v(112.75, 25.52) * mm, "end": v(105.25, 25.52) * mm});
            skLineSegment(sketch, "E84.left", {"start": v(112.75, 39.52) * mm, "end": v(112.75, 37.47) * mm});
            skLineSegment(sketch, "E84.right", {"start": v(105.25, 39.52) * mm, "end": v(105.25, 37.47) * mm});
            skPoint(sketch, "E84.middle", {"position": v(109, 32.52) * mm});
            skLineSegment(sketch, "E85.bottom", {"start": v(142.75, 39.52) * mm, "end": v(135.25, 39.52) * mm});
            skLineSegment(sketch, "E85.top", {"start": v(142.75, 25.52) * mm, "end": v(135.25, 25.52) * mm});
            skLineSegment(sketch, "E85.left", {"start": v(142.75, 39.52) * mm, "end": v(142.75, 37.47) * mm});
            skLineSegment(sketch, "E85.right", {"start": v(135.25, 39.52) * mm, "end": v(135.25, 37.47) * mm});
            skPoint(sketch, "E85.middle", {"position": v(139, 32.52) * mm});
            skLineSegment(sketch, "E86", {"start": v(79, 32.52) * mm, "end": v(78, 32.52) * mm, "construction": true});
            skLineSegment(sketch, "E87", {"start": v(78, 32.52) * mm, "end": v(80, 32.52) * mm, "construction": true});
            skLineSegment(sketch, "E88", {"start": v(109, 32.52) * mm, "end": v(108, 32.52) * mm, "construction": true});
            skLineSegment(sketch, "E89", {"start": v(108, 32.52) * mm, "end": v(110, 32.52) * mm, "construction": true});
            skLineSegment(sketch, "E90", {"start": v(139, 32.52) * mm, "end": v(140, 32.52) * mm, "construction": true});
            skLineSegment(sketch, "E91", {"start": v(140, 32.52) * mm, "end": v(138, 32.52) * mm, "construction": true});
            skLineSegment(sketch, "E92", {"start": v(138, 32.52) * mm, "end": v(136, 32.52) * mm, "construction": true});
            skLineSegment(sketch, "E93", {"start": v(136, 32.52) * mm, "end": v(142, 32.52) * mm, "construction": true});
            skLineSegment(sketch, "E94", {"start": v(110, 32.52) * mm, "end": v(112, 32.52) * mm, "construction": true});
            skLineSegment(sketch, "E95", {"start": v(112, 32.52) * mm, "end": v(106, 32.52) * mm, "construction": true});
            skLineSegment(sketch, "E96", {"start": v(80, 32.52) * mm, "end": v(82, 32.52) * mm, "construction": true});
            skLineSegment(sketch, "E97", {"start": v(82, 32.52) * mm, "end": v(76, 32.52) * mm, "construction": true});
            skLineSegment(sketch, "E98", {"start": v(76, 32.52) * mm, "end": v(76, 41.52) * mm, "construction": true});
            skLineSegment(sketch, "E99", {"start": v(78, 23.52) * mm, "end": v(80, 23.52) * mm});
            skLineSegment(sketch, "E100.trimOffspring", {"start": v(112.75, 27.58) * mm, "end": v(112.75, 25.52) * mm});
            skLineSegment(sketch, "E101.trimOffspring", {"start": v(105.25, 27.58) * mm, "end": v(105.25, 25.52) * mm});
            skLineSegment(sketch, "E102.trimOffspring", {"start": v(135.25, 27.58) * mm, "end": v(135.25, 25.52) * mm});
            skLineSegment(sketch, "E103.trimOffspring", {"start": v(142.75, 27.58) * mm, "end": v(142.75, 25.52) * mm});
            skLineSegment(sketch, "E104.trimOffspring", {"start": v(75.25, 27.58) * mm, "end": v(75.25, 25.52) * mm});
            skLineSegment(sketch, "E105.trimOffspring", {"start": v(82.75, 27.58) * mm, "end": v(82.75, 25.52) * mm});
            skArc(sketch, "E106", {"start": v(78, 41.52) * mm, "mid": v(69, 32.52) * mm, "end": v(78, 23.52) * mm});
            skArc(sketch, "E107", {"start": v(80, 23.52) * mm, "mid": v(89, 32.52) * mm, "end": v(80, 41.52) * mm});
            skArc(sketch, "E108", {"start": v(108, 41.52) * mm, "mid": v(99, 32.52) * mm, "end": v(108, 23.52) * mm});
            skArc(sketch, "E109", {"start": v(110, 23.52) * mm, "mid": v(119, 32.52) * mm, "end": v(110, 41.52) * mm});
            skArc(sketch, "E110", {"start": v(138, 41.52) * mm, "mid": v(129, 32.52) * mm, "end": v(138, 23.52) * mm});
            skArc(sketch, "E111", {"start": v(140, 23.52) * mm, "mid": v(149, 32.52) * mm, "end": v(140, 41.52) * mm});
            skLineSegment(sketch, "E112", {"start": v(108, 23.52) * mm, "end": v(110, 23.52) * mm});
            skLineSegment(sketch, "E113", {"start": v(78, 41.52) * mm, "end": v(80, 41.52) * mm});
            skLineSegment(sketch, "E114.trimOffspring", {"start": v(108, 41.52) * mm, "end": v(110, 41.52) * mm});
            skLineSegment(sketch, "E115.trimOffspring", {"start": v(138, 41.52) * mm, "end": v(140, 41.52) * mm});
            skArc(sketch, "E116", {"start": v(142.75, 27.58) * mm, "mid": v(147, 32.52) * mm, "end": v(142.75, 37.47) * mm});
            skArc(sketch, "E117", {"start": v(136, 37.52) * mm, "mid": v(131.01, 32.9) * mm, "end": v(135.25, 27.58) * mm});
            skArc(sketch, "E118", {"start": v(112.75, 27.58) * mm, "mid": v(117, 32.52) * mm, "end": v(112.75, 37.47) * mm});
            skArc(sketch, "E119", {"start": v(105.25, 37.47) * mm, "mid": v(101, 32.52) * mm, "end": v(105.25, 27.58) * mm});
            skArc(sketch, "E120", {"start": v(82.75, 27.58) * mm, "mid": v(87, 32.52) * mm, "end": v(82.75, 37.47) * mm});
            skArc(sketch, "E121", {"start": v(75.25, 37.47) * mm, "mid": v(71, 32.52) * mm, "end": v(75.25, 27.58) * mm});
            skLineSegment(sketch, "E122", {"start": v(142, 37.52) * mm, "end": v(142, 27.52) * mm, "construction": true});
            skLineSegment(sketch, "E123", {"start": v(136, 27.52) * mm, "end": v(135.25, 27.52) * mm});
            skLineSegment(sketch, "E124.trimOffspring", {"start": v(82.75, 27.52) * mm, "end": v(82, 27.52) * mm});
            skLineSegment(sketch, "E125.trimOffspring", {"start": v(138, 23.52) * mm, "end": v(140, 23.52) * mm});
            skLineSegment(sketch, "E126.bottom", {"start": v(52.75, 26.5) * mm, "end": v(45.25, 26.5) * mm});
            skLineSegment(sketch, "E126.top", {"start": v(52.75, 40.5) * mm, "end": v(45.25, 40.5) * mm});
            skLineSegment(sketch, "E126.left", {"start": v(52.75, 26.5) * mm, "end": v(52.75, 27) * mm});
            skLineSegment(sketch, "E126.right", {"start": v(45.25, 26.5) * mm, "end": v(45.25, 27) * mm});
            skPoint(sketch, "E126.middle", {"position": v(49, 33.5) * mm});
            skLineSegment(sketch, "E127", {"start": v(45.25, 26.5) * mm, "end": v(45.25, 27) * mm, "construction": true});
            skLineSegment(sketch, "E128", {"start": v(45.25, 40.5) * mm, "end": v(49, 40.5) * mm, "construction": true});
            skLineSegment(sketch, "E129", {"start": v(49, 40.5) * mm, "end": v(49, 40) * mm, "construction": true});
            skLineSegment(sketch, "E130", {"start": v(43, 40) * mm, "end": v(45.25, 40) * mm, "construction": true});
            skLineSegment(sketch, "E131.trimOffspring", {"start": v(52.75, 40) * mm, "end": v(55, 40) * mm});
            skLineSegment(sketch, "E132.trimOffspring", {"start": v(52.75, 27) * mm, "end": v(53.5, 27) * mm});
            skLineSegment(sketch, "E133.trimOffspring", {"start": v(45.25, 40) * mm, "end": v(45.25, 40.5) * mm});
            skLineSegment(sketch, "E134.trimOffspring", {"start": v(52.75, 40) * mm, "end": v(52.75, 40.5) * mm});
            skSolve(sketch);
        }
        {
            var Q0;
            Q0=makeQuery(id+"F17.imprint","IMPRINT",FACE,{"disambiguationData":[TD([[makeQuery(id+"F17.imprint","IMPRINT",EDGE,{"derivedFrom":sQuery(id+"F17.wireOp",EDGE,"E69.bottom")}),1.0]])]});
            var Q1;
            Q1=makeQuery(id+"F17.imprint","IMPRINT",FACE,{"disambiguationData":[TD([[makeQuery(id+"F17.imprint","IMPRINT",EDGE,{"derivedFrom":sQuery(id+"F17.wireOp",EDGE,"E83.bottom")}),1.0]])]});
            var Q2;
            Q2=makeQuery(id+"F17.imprint","IMPRINT",FACE,{"disambiguationData":[TD([[makeQuery(id+"F17.imprint","IMPRINT",EDGE,{"derivedFrom":sQuery(id+"F17.wireOp",EDGE,"E84.bottom")}),1.0]])]});
            var Q3;
            Q3=makeQuery(id+"F17.imprint","IMPRINT",FACE,{"disambiguationData":[TD([[makeQuery(id+"F17.imprint","IMPRINT",EDGE,{"derivedFrom":sQuery(id+"F17.wireOp",EDGE,"E85.bottom")}),1.0]])]});
            extrude(context, id + "F18", {"entities" : qUnion([Q0, Q1, Q2, Q3]), "operationType" : NewBodyOperationType.REMOVE, "oppositeDirection" : true, "depth" : 19 * mm});
        }
        {
            var Q0;
            Q0=makeQuery(id+"F17.imprint","IMPRINT",FACE,{"disambiguationData":[TD([[makeQuery(id+"F17.imprint","IMPRINT",EDGE,{"derivedFrom":sQuery(id+"F17.wireOp",EDGE,"E69.bottom")}),-1.0]])]});
            var Q1;
            Q1=makeQuery(id+"F17.imprint","IMPRINT",FACE,{"disambiguationData":[TD([[makeQuery(id+"F17.imprint","IMPRINT",EDGE,{"derivedFrom":sQuery(id+"F17.wireOp",EDGE,"E83.bottom")}),-1.0]])]});
            var Q2;
            Q2=makeQuery(id+"F17.imprint","IMPRINT",FACE,{"disambiguationData":[TD([[makeQuery(id+"F17.imprint","IMPRINT",EDGE,{"derivedFrom":sQuery(id+"F17.wireOp",EDGE,"E84.bottom")}),-1.0]])]});
            var Q3;
            Q3=makeQuery(id+"F17.imprint","IMPRINT",FACE,{"disambiguationData":[TD([[makeQuery(id+"F17.imprint","IMPRINT",EDGE,{"derivedFrom":sQuery(id+"F17.wireOp",EDGE,"E85.bottom")}),-1.0]])]});
            extrude(context, id + "F19", {"entities" : qUnion([Q0, Q1, Q2, Q3]), "operationType" : NewBodyOperationType.ADD, "depth" : 1 * mm});
        }
        {
            var Q0;
            Q0=makeQuery(id+"F1.opExtrude","CAP_FACE",FACE,{"disambiguationData":[OSD([sQuery(id+"F0.wireOp",EDGE,"E0.bottom"),sQuery(id+"F0.wireOp",EDGE,"E0.top"),sQuery(id+"F0.wireOp",EDGE,"E0.left"),sQuery(id+"F0.wireOp",EDGE,"E0.right"),sQuery(id+"F0.wireOp",EDGE,"E1.filletArc"),sQuery(id+"F0.wireOp",EDGE,"E2.filletArc"),sQuery(id+"F0.wireOp",EDGE,"E3.filletArc"),sQuery(id+"F0.wireOp",EDGE,"E4.filletArc"),sQuery(id+"F0.wireOp",EDGE,"E6")])],"isStart":false});
            var sketch = newSketch(context, id + "F20", { "sketchPlane" : qUnion([Q0])});
            skLineSegment(sketch, "E135.bottom", {"start": v(0, 0) * mm, "end": v(158, 0) * mm, "construction": true});
            skLineSegment(sketch, "E135.top", {"start": v(0, 32) * mm, "end": v(158, 32) * mm, "construction": true});
            skLineSegment(sketch, "E135.left", {"start": v(0, 0) * mm, "end": v(0, 32) * mm, "construction": true});
            skLineSegment(sketch, "E135.right", {"start": v(158, 0) * mm, "end": v(158, 32) * mm, "construction": true});
            skLineSegment(sketch, "E136", {"start": v(158, 32) * mm, "end": v(173, 32) * mm, "construction": true});
            skLineSegment(sketch, "E137", {"start": v(173, 32) * mm, "end": v(188, 32) * mm, "construction": true});
            skLineSegment(sketch, "E138", {"start": v(188, 32) * mm, "end": v(188, 12) * mm, "construction": true});
            skLineSegment(sketch, "E139", {"start": v(188, 12) * mm, "end": v(173, 12) * mm, "construction": true});
            skLineSegment(sketch, "E140", {"start": v(173, 12) * mm, "end": v(158, 12) * mm, "construction": true});
            skCircle(sketch, "E141", {"center": v(158, 32) * mm, "radius": 6 * mm});
            skCircle(sketch, "E142", {"center": v(158, 12) * mm, "radius": 5.8 * mm});
            skCircle(sketch, "E143", {"center": v(173, 12) * mm, "radius": 5.8 * mm});
            skCircle(sketch, "E144", {"center": v(188, 12) * mm, "radius": 5.8 * mm});
            skCircle(sketch, "E145", {"center": v(173, 32) * mm, "radius": 6 * mm});
            skCircle(sketch, "E146", {"center": v(188, 32) * mm, "radius": 6 * mm});
            skCircle(sketch, "E147", {"center": v(158, 12) * mm, "radius": 3 * mm});
            skCircle(sketch, "E148", {"center": v(173, 12) * mm, "radius": 3 * mm});
            skCircle(sketch, "E149", {"center": v(188, 12) * mm, "radius": 3 * mm});
            skLineSegment(sketch, "E150.bottom", {"start": v(160.75, 29.25) * mm, "end": v(155.25, 29.25) * mm});
            skLineSegment(sketch, "E150.top", {"start": v(160.75, 34.75) * mm, "end": v(155.25, 34.75) * mm});
            skLineSegment(sketch, "E150.left", {"start": v(160.75, 29.25) * mm, "end": v(160.75, 34.75) * mm});
            skLineSegment(sketch, "E150.right", {"start": v(155.25, 29.25) * mm, "end": v(155.25, 34.75) * mm});
            skLineSegment(sketch, "E151.bottom", {"start": v(175.75, 34.75) * mm, "end": v(170.25, 34.75) * mm});
            skLineSegment(sketch, "E151.top", {"start": v(175.75, 29.25) * mm, "end": v(170.25, 29.25) * mm});
            skLineSegment(sketch, "E151.left", {"start": v(175.75, 34.75) * mm, "end": v(175.75, 29.25) * mm});
            skLineSegment(sketch, "E151.right", {"start": v(170.25, 34.75) * mm, "end": v(170.25, 29.25) * mm});
            skLineSegment(sketch, "E152.bottom", {"start": v(190.75, 34.75) * mm, "end": v(185.25, 34.75) * mm});
            skLineSegment(sketch, "E152.top", {"start": v(190.75, 29.25) * mm, "end": v(185.25, 29.25) * mm});
            skLineSegment(sketch, "E152.left", {"start": v(190.75, 34.75) * mm, "end": v(190.75, 29.25) * mm});
            skLineSegment(sketch, "E152.right", {"start": v(185.25, 34.75) * mm, "end": v(185.25, 29.25) * mm});
            skSolve(sketch);
        }
        {
            var Q0;
            Q0=makeQuery(id+"F20.imprint","IMPRINT",FACE,{"disambiguationData":[TD([[makeQuery(id+"F20.imprint","IMPRINT",EDGE,{"derivedFrom":sQuery(id+"F20.wireOp",EDGE,"E141")}),1.0]])]});
            var Q1;
            Q1=makeQuery(id+"F20.imprint","IMPRINT",FACE,{"disambiguationData":[TD([[makeQuery(id+"F20.imprint","IMPRINT",EDGE,{"derivedFrom":sQuery(id+"F20.wireOp",EDGE,"E145")}),1.0]])]});
            var Q2;
            Q2=makeQuery(id+"F20.imprint","IMPRINT",FACE,{"disambiguationData":[TD([[makeQuery(id+"F20.imprint","IMPRINT",EDGE,{"derivedFrom":sQuery(id+"F20.wireOp",EDGE,"E146")}),1.0]])]});
            var Q3;
            {var subQ0=sQuery(id+"F20.wireOp",EDGE,"E144");var subQ1=sQuery(id+"F20.wireOp",EDGE,"E138");var subQ2=makeQuery(id+"F20.imprint","INTERSECT",VERTEX,{"derivedFrom":[subQ1,subQ0]});Q3=makeQuery(id+"F20.imprint","IMPRINT",FACE,{"disambiguationData":[TD([[makeQuery(id+"F20.imprint","IMPRINT",EDGE,{"disambiguationData":[TD([[subQ2,-1.0]])],"derivedFrom":subQ1}),1.0]])]});}
            var Q4;
            {var subQ0=sQuery(id+"F20.wireOp",EDGE,"E144");var subQ1=sQuery(id+"F20.wireOp",EDGE,"E138");var subQ2=makeQuery(id+"F20.imprint","INTERSECT",VERTEX,{"derivedFrom":[subQ1,subQ0]});Q4=makeQuery(id+"F20.imprint","IMPRINT",FACE,{"disambiguationData":[TD([[makeQuery(id+"F20.imprint","IMPRINT",EDGE,{"disambiguationData":[TD([[subQ2,-1.0]])],"derivedFrom":subQ1}),-1.0]])]});}
            var Q5;
            {var subQ0=sQuery(id+"F20.wireOp",EDGE,"E143");var subQ1=sQuery(id+"F20.wireOp",EDGE,"E139");var subQ2=makeQuery(id+"F20.imprint","INTERSECT",VERTEX,{"derivedFrom":[subQ1,subQ0]});Q5=makeQuery(id+"F20.imprint","IMPRINT",FACE,{"disambiguationData":[TD([[makeQuery(id+"F20.imprint","IMPRINT",EDGE,{"disambiguationData":[TD([[subQ2,-1.0]])],"derivedFrom":subQ1}),-1.0]])]});}
            var Q6;
            {var subQ0=sQuery(id+"F20.wireOp",EDGE,"E143");var subQ1=sQuery(id+"F20.wireOp",EDGE,"E139");var subQ2=makeQuery(id+"F20.imprint","INTERSECT",VERTEX,{"derivedFrom":[subQ1,subQ0]});Q6=makeQuery(id+"F20.imprint","IMPRINT",FACE,{"disambiguationData":[TD([[makeQuery(id+"F20.imprint","IMPRINT",EDGE,{"disambiguationData":[TD([[subQ2,-1.0]])],"derivedFrom":subQ1}),1.0]])]});}
            var Q7;
            Q7=makeQuery(id+"F20.imprint","IMPRINT",FACE,{"disambiguationData":[TD([[makeQuery(id+"F20.imprint","IMPRINT",EDGE,{"derivedFrom":sQuery(id+"F20.wireOp",EDGE,"E142")}),1.0]])]});
            var Q8;
            Q8=makeQuery(id+"F20.imprint","IMPRINT",FACE,{"disambiguationData":[TD([[makeQuery(id+"F20.imprint","IMPRINT",EDGE,{"derivedFrom":sQuery(id+"F20.wireOp",EDGE,"E143")}),1.0]])]});
            var Q9;
            Q9=makeQuery(id+"F20.imprint","IMPRINT",FACE,{"disambiguationData":[TD([[makeQuery(id+"F20.imprint","IMPRINT",EDGE,{"derivedFrom":sQuery(id+"F20.wireOp",EDGE,"E144")}),1.0]])]});
            extrude(context, id + "F21", {"entities" : qUnion([Q0, Q1, Q2, Q3, Q4, Q5, Q6, Q7, Q8, Q9]), "operationType" : NewBodyOperationType.ADD, "depth" : 1 * mm});
        }
        {
            var Q0;
            Q0=makeQuery(id+"F20.imprint","IMPRINT",FACE,{"disambiguationData":[TD([[makeQuery(id+"F20.imprint","IMPRINT",EDGE,{"derivedFrom":sQuery(id+"F20.wireOp",EDGE,"E150.bottom")}),-1.0]])]});
            var Q1;
            Q1=makeQuery(id+"F20.imprint","IMPRINT",FACE,{"disambiguationData":[TD([[makeQuery(id+"F20.imprint","IMPRINT",EDGE,{"derivedFrom":sQuery(id+"F20.wireOp",EDGE,"E151.bottom")}),1.0]])]});
            var Q2;
            Q2=makeQuery(id+"F20.imprint","IMPRINT",FACE,{"disambiguationData":[TD([[makeQuery(id+"F20.imprint","IMPRINT",EDGE,{"derivedFrom":sQuery(id+"F20.wireOp",EDGE,"E152.bottom")}),1.0]])]});
            extrude(context, id + "F22", {"entities" : qUnion([Q0, Q1, Q2]), "operationType" : NewBodyOperationType.REMOVE, "oppositeDirection" : true, "depth" : 8 * mm});
        }
        {
            var Q0;
            Q0=makeQuery(id+"F20.imprint","IMPRINT",FACE,{"disambiguationData":[TD([[makeQuery(id+"F20.imprint","IMPRINT",EDGE,{"derivedFrom":sQuery(id+"F20.wireOp",EDGE,"E147")}),1.0]])]});
            var Q1;
            Q1=makeQuery(id+"F20.imprint","IMPRINT",FACE,{"disambiguationData":[TD([[makeQuery(id+"F20.imprint","IMPRINT",EDGE,{"derivedFrom":sQuery(id+"F20.wireOp",EDGE,"E148")}),1.0]])]});
            var Q2;
            Q2=makeQuery(id+"F20.imprint","IMPRINT",FACE,{"disambiguationData":[TD([[makeQuery(id+"F20.imprint","IMPRINT",EDGE,{"derivedFrom":sQuery(id+"F20.wireOp",EDGE,"E149")}),1.0]])]});
            extrude(context, id + "F23", {"entities" : qUnion([Q0, Q1, Q2]), "operationType" : NewBodyOperationType.REMOVE, "oppositeDirection" : true, "depth" : 10.5 * mm});
        }
        {
            var Q0;
            Q0=makeQuery(id+"F1.opExtrude","CAP_FACE",FACE,{"disambiguationData":[OSD([sQuery(id+"F0.wireOp",EDGE,"E0.bottom"),sQuery(id+"F0.wireOp",EDGE,"E0.top"),sQuery(id+"F0.wireOp",EDGE,"E0.left"),sQuery(id+"F0.wireOp",EDGE,"E0.right"),sQuery(id+"F0.wireOp",EDGE,"E1.filletArc"),sQuery(id+"F0.wireOp",EDGE,"E2.filletArc"),sQuery(id+"F0.wireOp",EDGE,"E3.filletArc"),sQuery(id+"F0.wireOp",EDGE,"E4.filletArc"),sQuery(id+"F0.wireOp",EDGE,"E6")])],"isStart":true});
            var sketch = newSketch(context, id + "F24", { "sketchPlane" : qUnion([Q0])});
            skText(sketch, "E153", { "text": "876, 882", "fontName": "OpenSans-Regular.ttf"});
            skLineSegment(sketch, "E154.bottom", {"start": v(30, -5) * mm, "end": v(0, -5) * mm, "construction": true});
            skLineSegment(sketch, "E154.top", {"start": v(30, 0) * mm, "end": v(0, 0) * mm, "construction": true});
            skLineSegment(sketch, "E154.left", {"start": v(30, -5) * mm, "end": v(30, 0) * mm, "construction": true});
            skLineSegment(sketch, "E154.right", {"start": v(0, -5) * mm, "end": v(0, 0) * mm, "construction": true});
            const initialGuessF24  = {"E153": [0.03, -0.009, 1, 0, 0.004]};
            skSetInitialGuess(sketch, initialGuessF24);
            skSolve(sketch);
        }
        {
            var Q0;
            Q0 = qSketchRegion(id + "F24", true);
            extrude(context, id + "F25", {"entities" : qUnion([Q0]), "operationType" : NewBodyOperationType.REMOVE, "depth" : 1 * mm});
        }
    });
